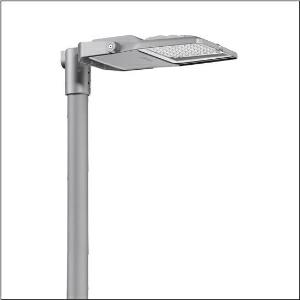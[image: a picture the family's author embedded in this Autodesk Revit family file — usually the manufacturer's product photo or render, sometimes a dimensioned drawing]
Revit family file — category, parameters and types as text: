
# Revit family: floodlight_fl_21_mini___pl61_5xa7776c2c3a_9e20
name_source: partatom
category: Lighting Fixtures
units: mm (PartAtom-declared; Revit-internal decimal feet)

## family parameters
Cut with Voids When Loaded = No
Host = Face
Light Source = No
Part Type = Normal
Room Calculation Point = No
Round Connector Dimension = Use Diameter
Shared = No

## types (1)
- --- (1 x LED, 11960 lm, 89 W, 3000K)
    Apparent Load = 89 VA
    CIE Flux Codes = 33 65 98 100 100
    Color Rendering = 70
    Color Temperature = 3000K
    Default Elevation = 1800 mm
    Description = Floodlight FL 21 mini, floodlight, primary light control with lens, of PMMA, primary optical cover: protective disc, of toughened safety glass, transparent, light distribution: PL61, light emission: direct distribution, installation type: surface-mounted, LED, High Power LED, rated luminous flux: 11.960lm, luminous efficacy: 134lm/W, light colour: 730, colour temperature: 3000K, control: flexible luminous flux parameterisation, time-dependent luminous flux control, constant luminous flux control, overheat protection, presetting dimming logarithmic, with terminal, 6-pole, mains connection: 220..240V, AC, 50/60Hz, start of lifetime: 89W, end of service life: 94W, reduction: 43W, luminaire housing, of diecast aluminium, powder-coated, Siteco® metallic grey (DB 702S), corrosivity category C5 mid according to DIN EN ISO 12944, sealing non-destructively replaceable, please order mast flange separately, mast bracket, of steel, galvanised, powder-coated, Siteco® metallic grey (DB 702S), Smart Interface below and above, protection rating (complete): IP66, insulation class (complete): insulation class II (safety insulation), certification: CE, ENEC, VDE, protection symbol: D, impact resistance: IK08, permissible operating ambient temperature: -40..+40°C, permissible operating ambient temperature for outdoor applications: -40..+50°C, standard: DIN EN 12944, LABS conformity tested according to VDMA 24364:2018-05, packaging unit: 1 piece

Light Distribution: PL61
    Height = 70 mm
    Lamp = 1 x LED
    Lamp Light Flux = 11960 lm
    Lamp Power = 89 W
    Lamp count = 1
    Length = 485 mm
    Luminous efficacy = 134 lm/W
    Manufacturer = Siteco
    ModVariant = No
    Model = 5XA7776C2C3A
    Number of Poles = 1
    OnlyDefault = Yes
    Power Factor = 1
    Product Name = Floodlight FL 21 mini | PL61
    Product group = floodlight | pylon annexe
    ProductGroupID = 6200
    Protection Class = Protection class II
    Protection Degree = IP 66
    RLX_Detail_Level = 1
    RLX_Emergency_Light_Flux = 0 lm
    RLX_Emergency_Type = 0
    RLX_Emergency_Type_DB = No
    RlxData = <blob elided: 100981 chars, md5=b4e420e4>
    Socket = socket
    Standby Power = 0 W
    System Light Flux = 11960 lm
    System Power = 89 W
    Type Comments = factory setting: luminous flux: 100 % | dim-lin: 254 | 456 mA
    Type Image = l_1007125.jpg
    URL = http://relux.com
    VarID = @adj_105073
    Voltage = 0 V
    Weight = 0.00 kg
    Width = 337 mm

## geometry (parser evidence)
native form markers: Blend x4, Sweep x13
no freeform markers — native parametric forms only
